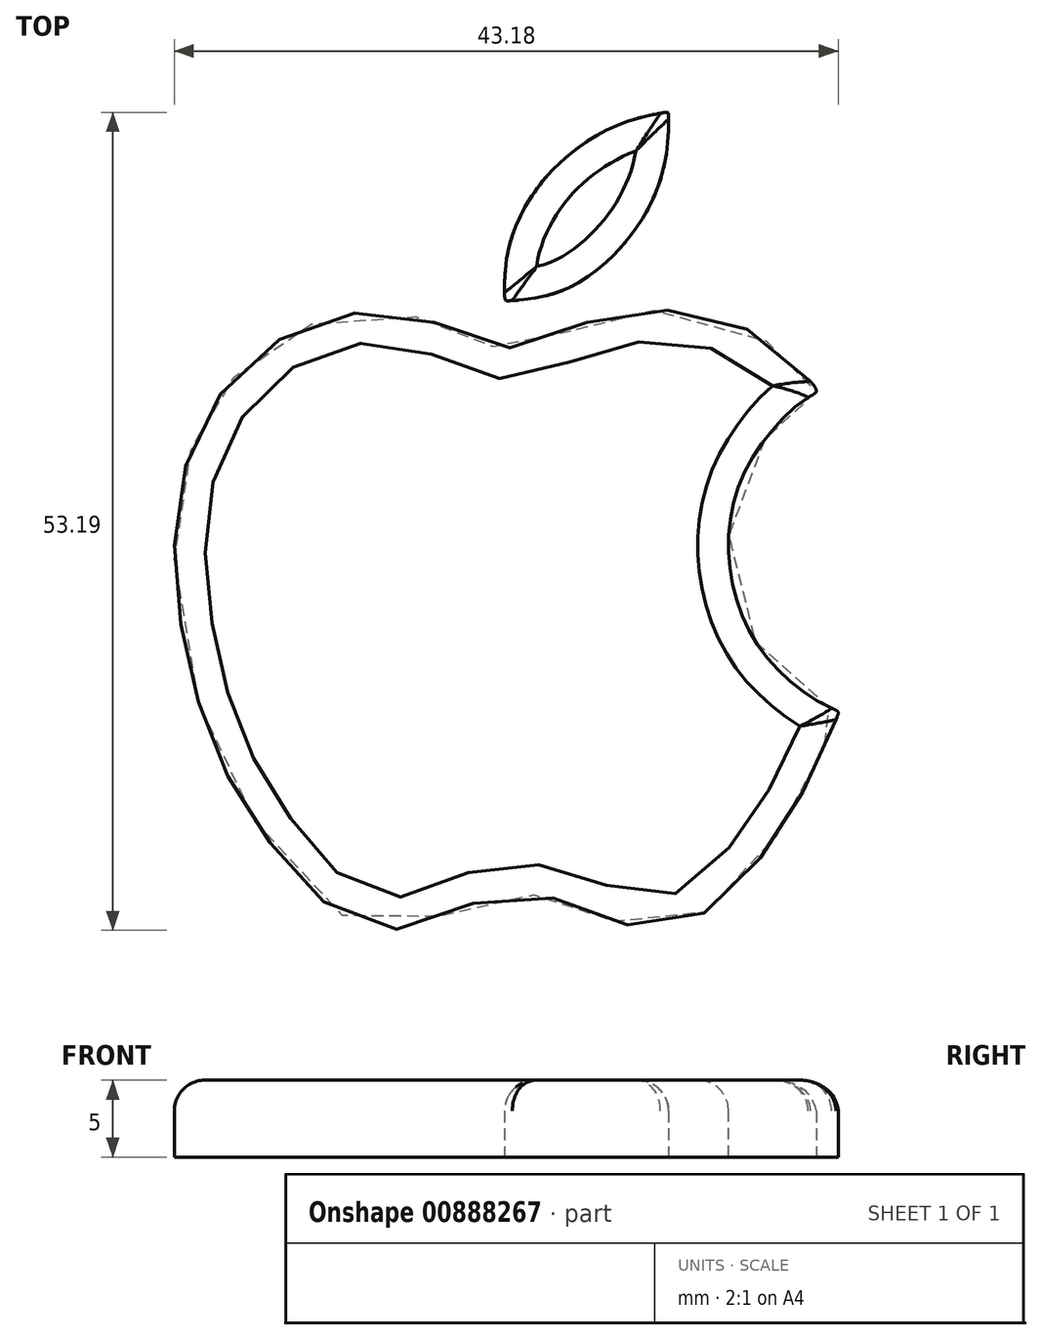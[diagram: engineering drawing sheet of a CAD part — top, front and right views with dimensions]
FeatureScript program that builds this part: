
annotation { "Feature Type Name" : "Feature", "Feature Type Description" : "" }
export const myFeature = defineFeature(function(context is Context, id is Id, definition is map)
    precondition{}
    {
        {
            var Q0;
            Q0=qCreatedBy(makeId("Top.planeOp"),FACE);
            var sketch = newSketch(context, id + "F0", { "sketchPlane" : qUnion([Q0])});
            skFitSpline(sketch, "E0", {"points": [v(26.54, 40.92) * mm, v(26.47, 41.38) * mm, v(26.74, 44.25) * mm, v(29.36, 49.13) * mm, v(34, 52.36) * mm, v(36.55, 53.05) * mm, v(37.09, 53.1) * mm, v(37.14, 52.82) * mm, v(36.95, 50.18) * mm, v(35.04, 45.61) * mm, v(30.25, 41.54) * mm, v(26.83, 40.88) * mm, v(26.54, 40.92) * mm]});
            skFitSpline(sketch, "E1", {"points": [v(46.73, 34.95) * mm, v(46.06, 34.49) * mm, v(42.7, 30.83) * mm, v(41.04, 24.76) * mm, v(43.4, 17.82) * mm, v(47.62, 14.41) * mm, v(48.15, 14.14) * mm, v(48.02, 13.63) * mm, v(46.08, 9.32) * mm, v(42.89, 4.39) * mm, v(38.06, 0.34) * mm, v(33.14, 0.68) * mm, v(29.06, 2.13) * mm, v(23.51, 1.38) * mm, v(18, 0) * mm, v(11.37, 5.45) * mm, v(6.65, 14.47) * mm, v(5.04, 26.45) * mm, v(6.53, 32.21) * mm, v(8.77, 35.78) * mm, v(12.9, 38.92) * mm, v(19.32, 40.1) * mm, v(24.5, 38.36) * mm, v(26.54, 37.8) * mm, v(29.2, 38.42) * mm, v(33.88, 40.02) * mm, v(41.88, 39.18) * mm, v(46.27, 35.74) * mm, v(46.73, 34.95) * mm]});
            skSolve(sketch);
        }
        {
            var Q0;
            Q0=makeQuery(id+"F0.imprint","IMPRINT",FACE,{"disambiguationData":[TD([[makeQuery(id+"F0.imprint","IMPRINT",EDGE,{"derivedFrom":sQuery(id+"F0.wireOp",EDGE,"E1")}),-1.0]])]});
            var Q1;
            Q1=makeQuery(id+"F0.imprint","IMPRINT",FACE,{"disambiguationData":[TD([[makeQuery(id+"F0.imprint","IMPRINT",EDGE,{"derivedFrom":sQuery(id+"F0.wireOp",EDGE,"E0")}),-1.0]])]});
            extrude(context, id + "F1", {"entities" : qUnion([Q0, Q1]), "depth" : 5 * mm, "offsetDistance" : 25 * mm});
        }
        {
            var Q0;
            Q0=makeQuery(id+"F1.opExtrude","CAP_EDGE",EDGE,{"disambiguationData":[OSD([sQuery(id+"F0.wireOp",EDGE,"E1")])],"isStart":false});
            var Q1;
            Q1=makeQuery(id+"F1.opExtrude","CAP_EDGE",EDGE,{"disambiguationData":[OSD([sQuery(id+"F0.wireOp",EDGE,"E0")])],"isStart":false});
            fillet(context, id + "F2", {"entities" : qUnion([Q0, Q1]), "radius" : 2 * mm, "tangentPropagation" : true, "allowEdgeOverflow" : false});
        }
    });
